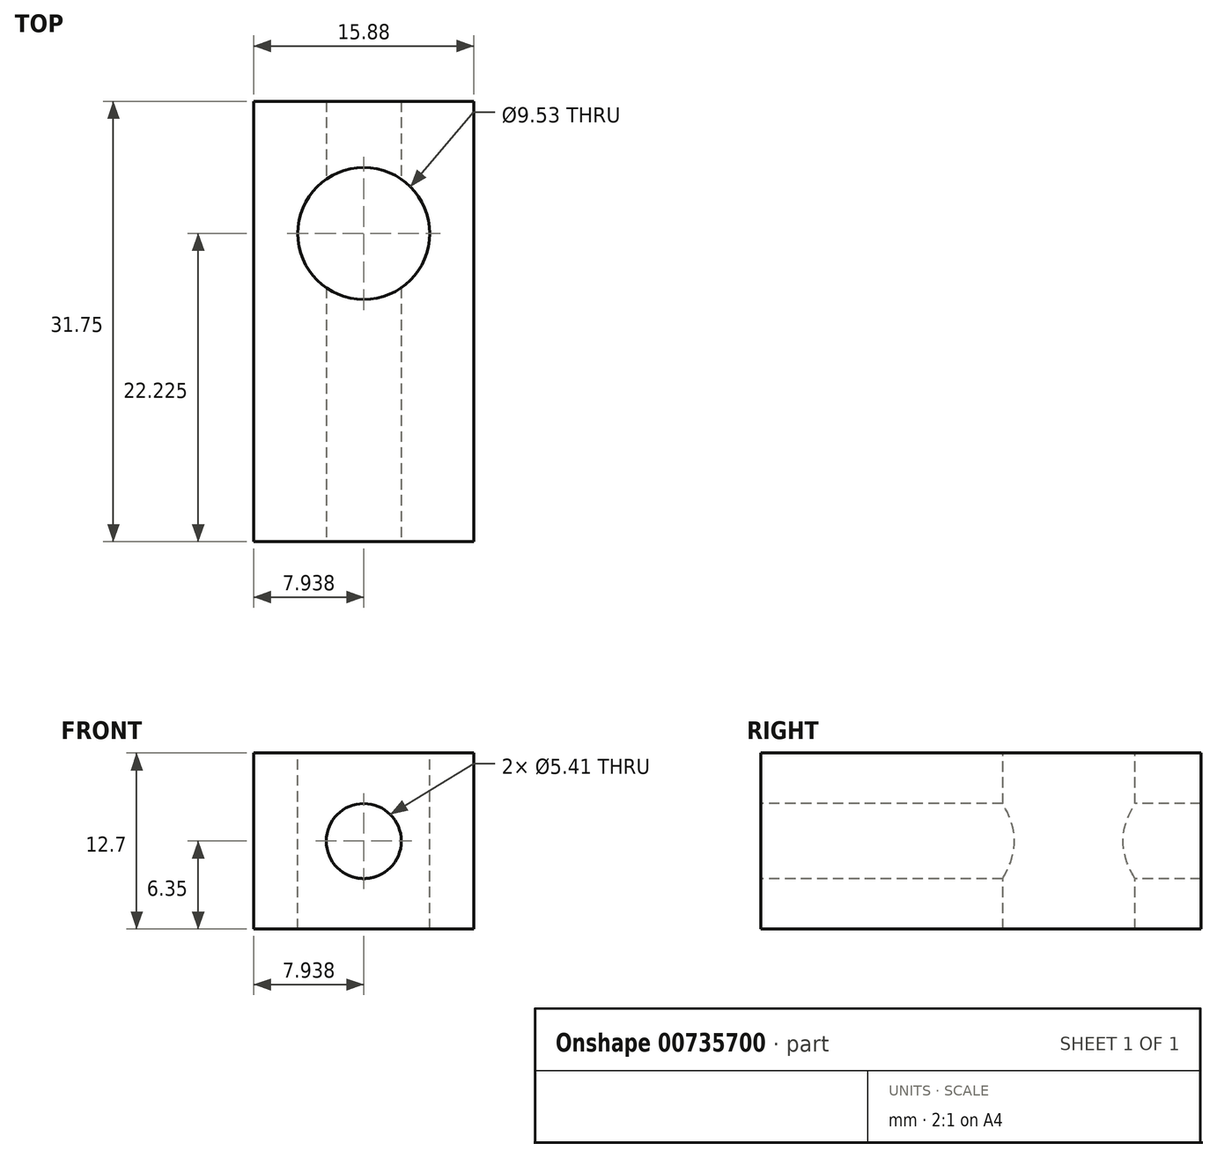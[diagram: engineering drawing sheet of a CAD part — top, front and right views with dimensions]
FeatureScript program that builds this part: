
annotation { "Feature Type Name" : "Feature", "Feature Type Description" : "" }
export const myFeature = defineFeature(function(context is Context, id is Id, definition is map)
    precondition{}
    {
        {
            var Q0;
            Q0=qCreatedBy(makeId("Top.planeOp"),FACE);
            var sketch = newSketch(context, id + "F0", { "sketchPlane" : qUnion([Q0])});
            skLineSegment(sketch, "E0.bottom", {"start": v(0, 0) * mm, "end": v(15.88, 0) * mm});
            skLineSegment(sketch, "E0.top", {"start": v(0, 31.75) * mm, "end": v(15.87, 31.75) * mm});
            skLineSegment(sketch, "E0.left", {"start": v(0, 0) * mm, "end": v(0, 31.75) * mm});
            skLineSegment(sketch, "E0.right", {"start": v(15.88, 0) * mm, "end": v(15.87, 31.75) * mm});
            skPoint(sketch, "E1.positionSnap0", {"position": v(7.94, 0) * mm});
            skSolve(sketch);
        }
        {
            var Q0;
            Q0 = qSketchRegion(id + "F0", true);
            extrude(context, id + "F1", {"entities" : qUnion([Q0]), "depth" : 12.7 * mm, "offsetDistance" : 25.4 * mm});
        }
        {
            var Q0;
            Q0=makeQuery(id+"F1.opExtrude","CAP_FACE",FACE,{"disambiguationData":[OSD([sQuery(id+"F0.wireOp",EDGE,"E0.bottom"),sQuery(id+"F0.wireOp",EDGE,"E0.top"),sQuery(id+"F0.wireOp",EDGE,"E0.left"),sQuery(id+"F0.wireOp",EDGE,"E0.right")])],"isStart":false});
            var sketch = newSketch(context, id + "F2", { "sketchPlane" : qUnion([Q0])});
            skPoint(sketch, "E2", {"position": v(7.94, 22.23) * mm});
            skPoint(sketch, "E2.positionSnap0", {"position": v(7.94, 0) * mm});
            skCircle(sketch, "E3", {"center": v(7.94, 22.23) * mm, "radius": 4.76 * mm});
            skSolve(sketch);
        }
        {
            var Q0;
            Q0=makeQuery(id+"F2.imprint","IMPRINT",FACE,{"disambiguationData":[TD([[makeQuery(id+"F2.imprint","IMPRINT",EDGE,{"derivedFrom":sQuery(id+"F2.wireOp",EDGE,"E3")}),1.0]])]});
            var Q1;
            Q1=sQuery(id+"F2.wireOp",EDGE,"E3");
            extrude(context, id + "F3", {"entities" : qUnion([Q0]), "operationType" : NewBodyOperationType.REMOVE, "surfaceEntities" : qUnion([Q1]), "endBound" : BoundingType.UP_TO_NEXT, "oppositeDirection" : true, "depth" : 25.4 * mm, "offsetDistance" : 25.4 * mm});
        }
        {
            var Q0;
            Q0=makeQuery(id+"F1.opExtrude","SWEPT_FACE",FACE,{"disambiguationData":[OSD([sQuery(id+"F0.wireOp",EDGE,"E0.bottom")])]});
            var sketch = newSketch(context, id + "F4", { "sketchPlane" : qUnion([Q0])});
            skPoint(sketch, "E4", {"position": v(7.94, 6.35) * mm});
            skPoint(sketch, "E4.positionSnap0", {"position": v(0, 6.35) * mm});
            skPoint(sketch, "E4.positionSnap1", {"position": v(7.94, 12.7) * mm});
            skCircle(sketch, "E5", {"center": v(7.94, 6.35) * mm, "radius": 2.7 * mm});
            skSolve(sketch);
        }
        {
            var Q0;
            Q0 = qSketchRegion(id + "F4", true);
            var Q1;
            Q1=makeQuery(id+"F1.opExtrude","SWEPT_FACE",FACE,{"disambiguationData":[OSD([sQuery(id+"F0.wireOp",EDGE,"E0.top")])]});
            extrude(context, id + "F5", {"entities" : qUnion([Q0]), "operationType" : NewBodyOperationType.REMOVE, "endBound" : BoundingType.UP_TO_SURFACE, "oppositeDirection" : true, "depth" : 25.4 * mm, "endBoundEntityFace" : qUnion([Q1]), "offsetDistance" : 25.4 * mm});
        }
    });
